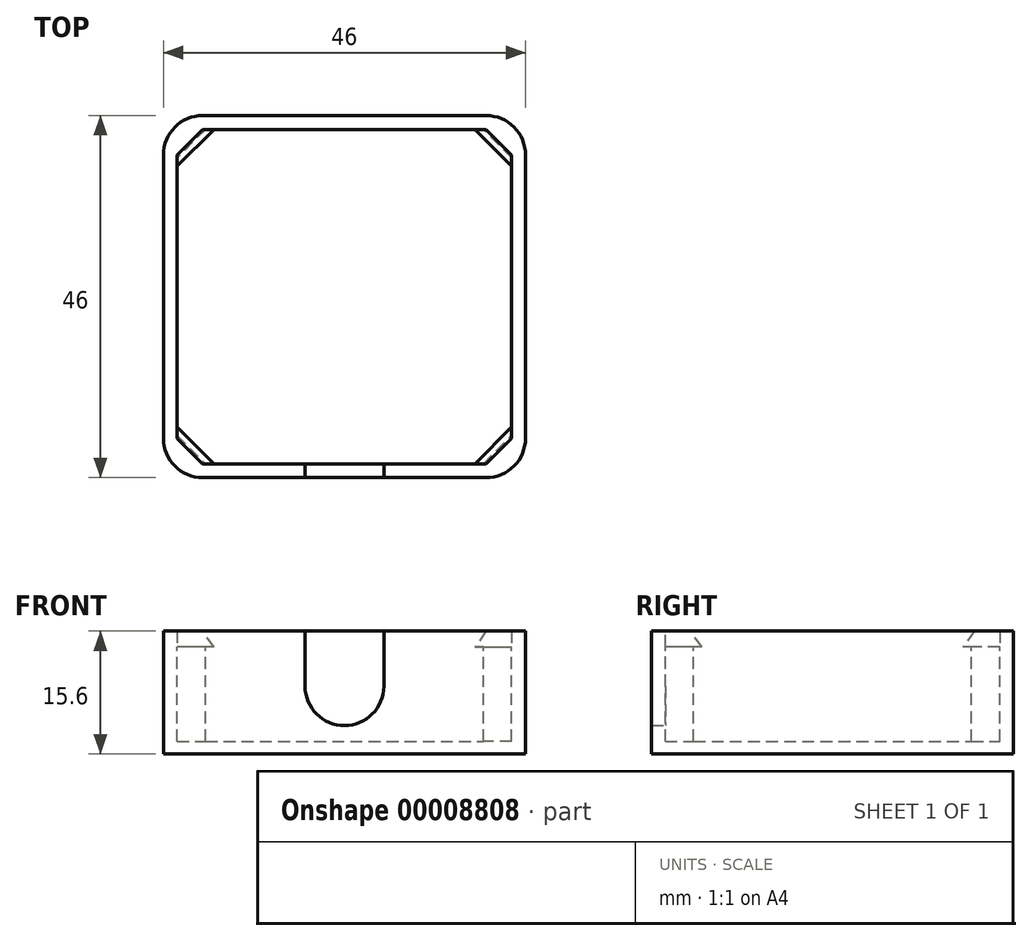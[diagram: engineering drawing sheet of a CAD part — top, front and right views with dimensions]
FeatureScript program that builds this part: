
annotation { "Feature Type Name" : "Feature", "Feature Type Description" : "" }
export const myFeature = defineFeature(function(context is Context, id is Id, definition is map)
    precondition{}
    {
        {
            var Q0;
            Q0=qCreatedBy(makeId("Top.planeOp"),FACE);
            var sketch = newSketch(context, id + "F0", { "sketchPlane" : qUnion([Q0])});
            skLineSegment(sketch, "E0.bottom", {"start": v(-23, 23) * mm, "end": v(23, 23) * mm});
            skLineSegment(sketch, "E0.top", {"start": v(-23, -23) * mm, "end": v(23, -23) * mm});
            skLineSegment(sketch, "E0.left", {"start": v(-23, 23) * mm, "end": v(-23, -23) * mm});
            skLineSegment(sketch, "E0.right", {"start": v(23, 23) * mm, "end": v(23, -23) * mm});
            skLineSegment(sketch, "E1", {"start": v(-23, 23) * mm, "end": v(23, -23) * mm, "construction": true});
            skLineSegment(sketch, "E2", {"start": v(23, 23) * mm, "end": v(-23, -23) * mm, "construction": true});
            skSolve(sketch);
        }
        {
            var Q0;
            Q0=makeQuery(id+"F0.imprint","IMPRINT",FACE,{"disambiguationData":[TD([[makeQuery(id+"F0.imprint","IMPRINT",EDGE,{"derivedFrom":sQuery(id+"F0.wireOp",EDGE,"E0.bottom")}),-1.0]])]});
            extrude(context, id + "F1", {"entities" : qUnion([Q0]), "depth" : 15.6 * mm});
        }
        {
            var Q0;
            Q0=makeQuery(id+"F1.opExtrude","CAP_FACE",FACE,{"disambiguationData":[OSD([sQuery(id+"F0.wireOp",EDGE,"E0.bottom"),sQuery(id+"F0.wireOp",EDGE,"E0.top"),sQuery(id+"F0.wireOp",EDGE,"E0.left"),sQuery(id+"F0.wireOp",EDGE,"E0.right")])],"isStart":false});
            var sketch = newSketch(context, id + "F2", { "sketchPlane" : qUnion([Q0])});
            skLineSegment(sketch, "E3", {"start": v(-17.64, 21.25) * mm, "end": v(17.64, 21.25) * mm});
            skLineSegment(sketch, "E4", {"start": v(17.64, 21.25) * mm, "end": v(21.25, 17.64) * mm});
            skLineSegment(sketch, "E5", {"start": v(21.25, 17.64) * mm, "end": v(21.25, -17.64) * mm});
            skLineSegment(sketch, "E6", {"start": v(21.25, -17.64) * mm, "end": v(17.64, -21.25) * mm});
            skLineSegment(sketch, "E7", {"start": v(17.64, -21.25) * mm, "end": v(-17.64, -21.25) * mm});
            skLineSegment(sketch, "E8", {"start": v(-17.64, -21.25) * mm, "end": v(-21.25, -17.64) * mm});
            skLineSegment(sketch, "E9", {"start": v(-21.25, -17.64) * mm, "end": v(-21.25, 17.64) * mm});
            skLineSegment(sketch, "E10", {"start": v(-21.25, 17.64) * mm, "end": v(-17.64, 21.25) * mm});
            skLineSegment(sketch, "E11", {"start": v(-17.64, 21.25) * mm, "end": v(21.25, -17.64) * mm, "construction": true});
            skLineSegment(sketch, "E12", {"start": v(17.64, -21.25) * mm, "end": v(-21.25, 17.64) * mm, "construction": true});
            skLineSegment(sketch, "E13", {"start": v(17.64, 21.25) * mm, "end": v(-21.25, -17.64) * mm, "construction": true});
            skLineSegment(sketch, "E14", {"start": v(-17.64, -21.25) * mm, "end": v(21.25, 17.64) * mm, "construction": true});
            skLineSegment(sketch, "E15", {"start": v(-21.25, 0) * mm, "end": v(21.25, 0) * mm, "construction": true});
            skSolve(sketch);
        }
        {
            var Q0;
            Q0=makeQuery(id+"F2.imprint","IMPRINT",FACE,{"disambiguationData":[TD([[makeQuery(id+"F2.imprint","IMPRINT",EDGE,{"derivedFrom":sQuery(id+"F2.wireOp",EDGE,"E3")}),-1.0]])]});
            extrude(context, id + "F3", {"entities" : qUnion([Q0]), "operationType" : NewBodyOperationType.REMOVE, "oppositeDirection" : true, "depth" : 14 * mm});
        }
        {
            var Q0;
            Q0=makeQuery(id+"F1.opExtrude","CAP_FACE",FACE,{"disambiguationData":[OSD([sQuery(id+"F0.wireOp",EDGE,"E0.bottom"),sQuery(id+"F0.wireOp",EDGE,"E0.top"),sQuery(id+"F0.wireOp",EDGE,"E0.left"),sQuery(id+"F0.wireOp",EDGE,"E0.right")])],"isStart":false});
            var sketch = newSketch(context, id + "F4", { "sketchPlane" : qUnion([Q0])});
            skLineSegment(sketch, "E16", {"start": v(-16.58, 21.25) * mm, "end": v(16.58, 21.25) * mm});
            skLineSegment(sketch, "E17", {"start": v(16.58, 21.25) * mm, "end": v(21.25, 16.58) * mm});
            skLineSegment(sketch, "E18", {"start": v(21.25, 16.58) * mm, "end": v(21.25, -16.58) * mm});
            skLineSegment(sketch, "E19", {"start": v(21.25, -16.58) * mm, "end": v(16.58, -21.25) * mm});
            skLineSegment(sketch, "E20", {"start": v(16.58, -21.25) * mm, "end": v(-16.58, -21.25) * mm});
            skLineSegment(sketch, "E21", {"start": v(-16.58, -21.25) * mm, "end": v(-21.25, -16.58) * mm});
            skLineSegment(sketch, "E22", {"start": v(-21.25, -16.58) * mm, "end": v(-21.25, 16.58) * mm});
            skLineSegment(sketch, "E23", {"start": v(-21.25, 16.58) * mm, "end": v(-16.58, 21.25) * mm});
            skLineSegment(sketch, "E24", {"start": v(0, 21.25) * mm, "end": v(0, -21.25) * mm, "construction": true});
            skLineSegment(sketch, "E25", {"start": v(21.25, 0) * mm, "end": v(-21.25, 0) * mm, "construction": true});
            skLineSegment(sketch, "E26.bottom", {"start": v(-23, 23) * mm, "end": v(23, 23) * mm, "construction": true});
            skLineSegment(sketch, "E26.top", {"start": v(-23, -23) * mm, "end": v(23, -23) * mm, "construction": true});
            skLineSegment(sketch, "E26.left", {"start": v(-23, 23) * mm, "end": v(-23, -23) * mm, "construction": true});
            skLineSegment(sketch, "E26.right", {"start": v(23, 23) * mm, "end": v(23, -23) * mm, "construction": true});
            skLineSegment(sketch, "E27.bottom", {"start": v(23, 23) * mm, "end": v(-23, 23) * mm});
            skLineSegment(sketch, "E27.top", {"start": v(23, -23) * mm, "end": v(-23, -23) * mm});
            skLineSegment(sketch, "E27.left", {"start": v(23, 23) * mm, "end": v(23, -23) * mm});
            skLineSegment(sketch, "E27.right", {"start": v(-23, 23) * mm, "end": v(-23, -23) * mm});
            skSolve(sketch);
        }
        {
            var Q0;
            Q0 = qSketchRegion(id + "F4", true);
            extrude(context, id + "F5", {"entities" : qUnion([Q0]), "operationType" : NewBodyOperationType.ADD, "oppositeDirection" : true, "depth" : 2 * mm});
        }
        {
            var Q0;
            Q0=makeQuery(id+"F5.opExtrude","CAP_EDGE",EDGE,{"disambiguationData":[OSD([sQuery(id+"F4.wireOp",EDGE,"E17")])],"isStart":true});
            var Q1;
            Q1=makeQuery(id+"F5.opExtrude","CAP_EDGE",EDGE,{"disambiguationData":[OSD([sQuery(id+"F4.wireOp",EDGE,"E23")])],"isStart":true});
            var Q2;
            Q2=makeQuery(id+"F5.opExtrude","CAP_EDGE",EDGE,{"disambiguationData":[OSD([sQuery(id+"F4.wireOp",EDGE,"E21")])],"isStart":true});
            var Q3;
            Q3=makeQuery(id+"F5.opExtrude","CAP_EDGE",EDGE,{"disambiguationData":[OSD([sQuery(id+"F4.wireOp",EDGE,"E19")])],"isStart":true});
            chamfer(context, id + "F6", {"entities" : qUnion([Q0, Q1, Q2, Q3]), "chamferType" : ChamferType.TWO_OFFSETS, "width1" : 1 * mm, "oppositeDirection" : false, "width2" : 2 * mm, "tangentPropagation" : true});
        }
        {
            var Q0;
            Q0=makeQuery(id+"F1.opExtrude","SWEPT_EDGE",EDGE,{"disambiguationData":[OSD([sQuery(id+"F0.wireOp",EDGE,"E0.bottom"),sQuery(id+"F0.wireOp",EDGE,"E0.left")])]});
            var Q1;
            Q1=makeQuery(id+"F1.opExtrude","SWEPT_EDGE",EDGE,{"disambiguationData":[OSD([sQuery(id+"F0.wireOp",EDGE,"E0.top"),sQuery(id+"F0.wireOp",EDGE,"E0.left")])]});
            var Q2;
            Q2=makeQuery(id+"F1.opExtrude","SWEPT_EDGE",EDGE,{"disambiguationData":[OSD([sQuery(id+"F0.wireOp",EDGE,"E0.top"),sQuery(id+"F0.wireOp",EDGE,"E0.right")])]});
            var Q3;
            Q3=makeQuery(id+"F1.opExtrude","SWEPT_EDGE",EDGE,{"disambiguationData":[OSD([sQuery(id+"F0.wireOp",EDGE,"E0.bottom"),sQuery(id+"F0.wireOp",EDGE,"E0.right")])]});
            fillet(context, id + "F7", {"entities" : qUnion([Q0, Q1, Q2, Q3]), "radius" : 5 * mm, "tangentPropagation" : true, "allowEdgeOverflow" : false});
        }
        {
            var Q0;
            Q0=makeQuery(id+"F1.opExtrude","SWEPT_FACE",FACE,{"disambiguationData":[OSD([sQuery(id+"F0.wireOp",EDGE,"E0.top")])]});
            var sketch = newSketch(context, id + "F8", { "sketchPlane" : qUnion([Q0])});
            skLineSegment(sketch, "E28.bottom", {"start": v(-5, 15.6) * mm, "end": v(5, 15.6) * mm});
            skLineSegment(sketch, "E28.top", {"start": v(-5, 3.6) * mm, "end": v(5, 3.6) * mm});
            skLineSegment(sketch, "E28.left", {"start": v(-5, 15.6) * mm, "end": v(-5, 3.6) * mm});
            skLineSegment(sketch, "E28.right", {"start": v(5, 15.6) * mm, "end": v(5, 3.6) * mm});
            skSolve(sketch);
        }
        {
            var Q0;
            Q0=makeQuery(id+"F8.imprint","IMPRINT",FACE,{"disambiguationData":[TD([[makeQuery(id+"F8.imprint","IMPRINT",EDGE,{"derivedFrom":sQuery(id+"F8.wireOp",EDGE,"E28.bottom")}),-1.0]])]});
            extrude(context, id + "F9", {"entities" : qUnion([Q0]), "operationType" : NewBodyOperationType.REMOVE, "oppositeDirection" : true, "depth" : 25 * mm});
        }
        {
            var Q0;
            Q0=makeQuery(id+"F9.boolean.opBoolean","COPY",EDGE,{"derivedFrom":makeQuery(id+"F9.opExtrude","SWEPT_EDGE",EDGE,{"disambiguationData":[OSD([sQuery(id+"F0.wireOp",EDGE,"E0.top"),sQuery(id+"F8.wireOp",EDGE,"E28.bottom"),sQuery(id+"F8.wireOp",EDGE,"E28.left")])]})});
            var Q1;
            Q1=makeQuery(id+"F9.boolean.opBoolean","COPY",EDGE,{"derivedFrom":makeQuery(id+"F9.opExtrude","SWEPT_EDGE",EDGE,{"disambiguationData":[OSD([sQuery(id+"F0.wireOp",EDGE,"E0.top"),sQuery(id+"F8.wireOp",EDGE,"E28.bottom"),sQuery(id+"F8.wireOp",EDGE,"E28.right")])]})});
            var Q2;
            Q2=makeQuery(id+"F9.boolean.opBoolean","COPY",EDGE,{"derivedFrom":makeQuery(id+"F9.opExtrude","SWEPT_EDGE",EDGE,{"disambiguationData":[OSD([sQuery(id+"F8.wireOp",EDGE,"E28.top"),sQuery(id+"F8.wireOp",EDGE,"E28.left")])]})});
            var Q3;
            Q3=makeQuery(id+"F9.boolean.opBoolean","COPY",EDGE,{"derivedFrom":makeQuery(id+"F9.opExtrude","SWEPT_EDGE",EDGE,{"disambiguationData":[OSD([sQuery(id+"F8.wireOp",EDGE,"E28.top"),sQuery(id+"F8.wireOp",EDGE,"E28.right")])]})});
            fillet(context, id + "F10", {"entities" : qUnion([Q0, Q1, Q2, Q3]), "radius" : 5 * mm, "tangentPropagation" : true, "allowEdgeOverflow" : false});
        }
    });
